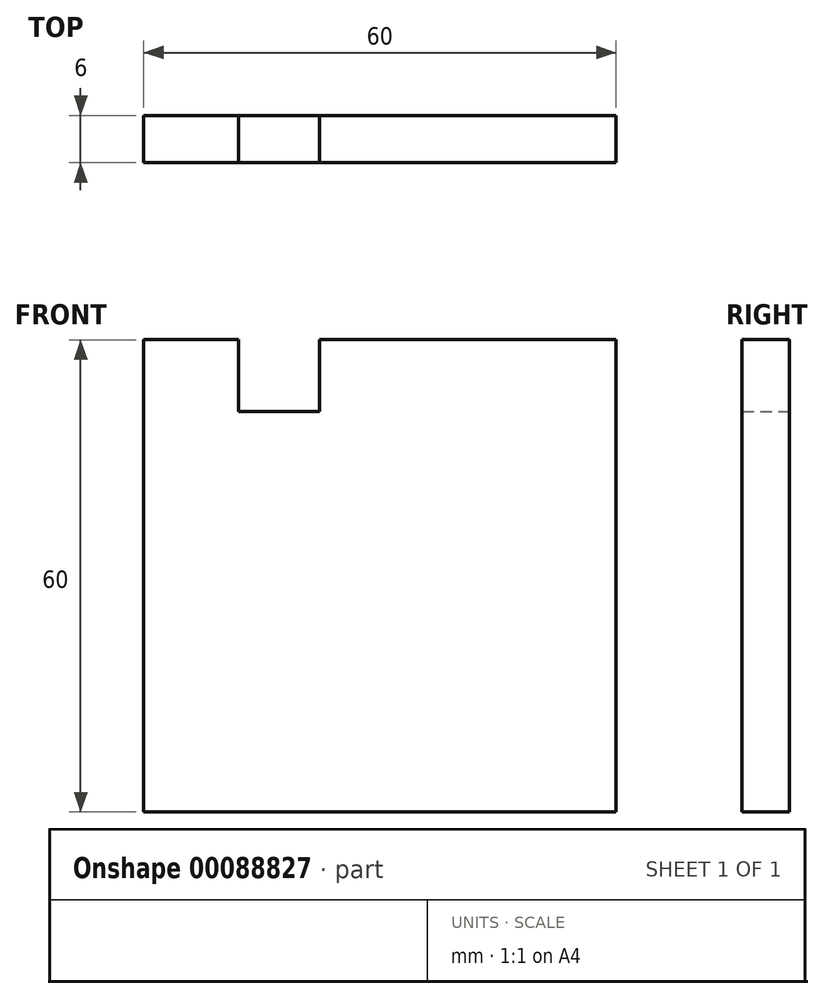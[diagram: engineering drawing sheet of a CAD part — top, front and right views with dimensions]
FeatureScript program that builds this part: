
annotation { "Feature Type Name" : "Feature", "Feature Type Description" : "" }
export const myFeature = defineFeature(function(context is Context, id is Id, definition is map)
    precondition{}
    {
        {
            var Q0;
            Q0=qCreatedBy(makeId("Front.planeOp"),FACE);
            var sketch = newSketch(context, id + "F0", { "sketchPlane" : qUnion([Q0])});
            skLineSegment(sketch, "E0.bottom", {"start": v(-38.26, 40.72) * mm, "end": v(21.74, 40.72) * mm});
            skLineSegment(sketch, "E0.top", {"start": v(-38.26, -19.28) * mm, "end": v(21.74, -19.28) * mm});
            skLineSegment(sketch, "E0.left", {"start": v(-38.26, 40.72) * mm, "end": v(-38.26, -19.28) * mm});
            skLineSegment(sketch, "E0.right", {"start": v(21.74, 40.72) * mm, "end": v(21.74, -19.28) * mm});
            skLineSegment(sketch, "E1.bottom", {"start": v(-26.2, 46.7) * mm, "end": v(-15.95, 46.7) * mm});
            skLineSegment(sketch, "E1.top", {"start": v(-26.2, 31.6) * mm, "end": v(-15.95, 31.6) * mm});
            skLineSegment(sketch, "E1.left", {"start": v(-26.2, 46.7) * mm, "end": v(-26.2, 31.6) * mm});
            skLineSegment(sketch, "E1.right", {"start": v(-15.95, 46.7) * mm, "end": v(-15.95, 31.6) * mm});
            skSolve(sketch);
        }
        {
            var Q0;
            Q0=makeQuery(id+"F0.imprint","IMPRINT",FACE,{"disambiguationData":[TD([[makeQuery(id+"F0.imprint","IMPRINT",EDGE,{"derivedFrom":sQuery(id+"F0.wireOp",EDGE,"E0.top")}),1.0]])]});
            extrude(context, id + "F1", {"entities" : qUnion([Q0]), "depth" : 6 * mm});
        }
    });
